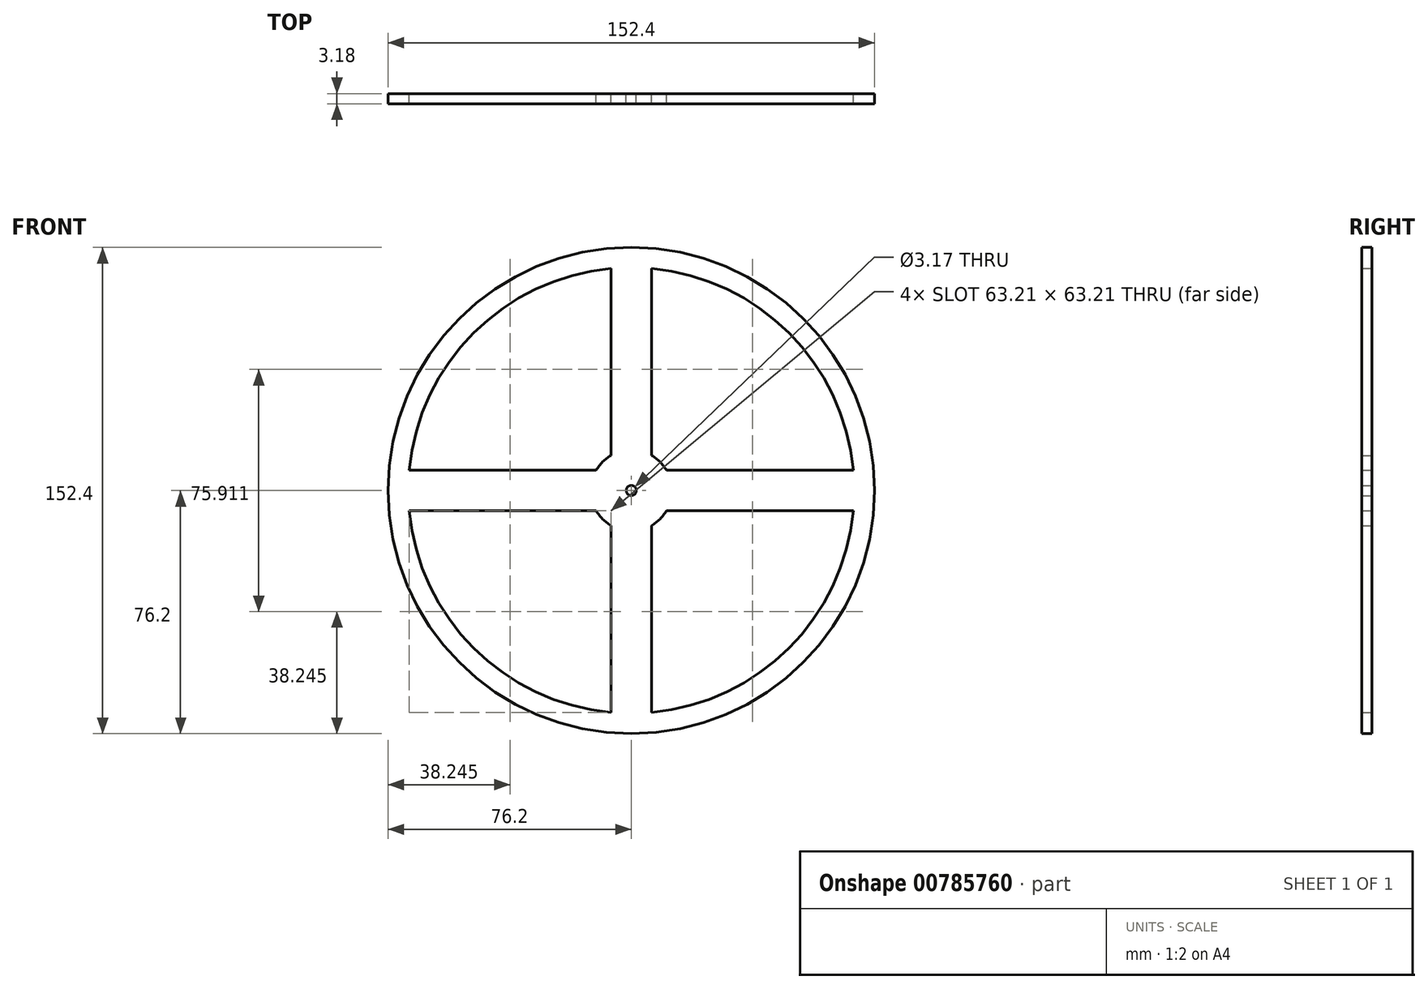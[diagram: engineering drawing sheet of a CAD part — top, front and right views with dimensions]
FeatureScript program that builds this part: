
annotation { "Feature Type Name" : "Feature", "Feature Type Description" : "" }
export const myFeature = defineFeature(function(context is Context, id is Id, definition is map)
    precondition{}
    {
        {
            var Q0;
            Q0=qCreatedBy(makeId("Front.planeOp"),FACE);
            var sketch = newSketch(context, id + "F0", { "sketchPlane" : qUnion([Q0])});
            skArc(sketch, "E0", {"start": v(-6.35, 69.56) * mm, "mid": v(-49.4, 49.4) * mm, "end": v(-69.56, 6.35) * mm});
            skCircle(sketch, "E1", {"center": v(0, 0) * mm, "radius": 1.59 * mm});
            skArc(sketch, "E2", {"start": v(-6.35, 11) * mm, "mid": v(-8.98, 8.98) * mm, "end": v(-11, 6.35) * mm});
            skLineSegment(sketch, "E3", {"start": v(-6.35, 69.56) * mm, "end": v(-6.35, 11) * mm});
            skLineSegment(sketch, "E4", {"start": v(6.35, 69.56) * mm, "end": v(6.35, 11) * mm});
            skLineSegment(sketch, "E5", {"start": v(-11, -6.35) * mm, "end": v(-69.56, -6.35) * mm});
            skLineSegment(sketch, "E6", {"start": v(-69.56, 6.35) * mm, "end": v(-69.56, -6.35) * mm, "construction": true});
            skLineSegment(sketch, "E7", {"start": v(-6.35, 69.56) * mm, "end": v(6.35, 69.56) * mm, "construction": true});
            skLineSegment(sketch, "E8", {"start": v(69.56, 6.35) * mm, "end": v(69.56, -6.35) * mm, "construction": true});
            skLineSegment(sketch, "E9", {"start": v(6.35, -69.56) * mm, "end": v(-6.35, -69.56) * mm, "construction": true});
            skLineSegment(sketch, "E10", {"start": v(-69.56, 6.35) * mm, "end": v(-11, 6.35) * mm});
            skLineSegment(sketch, "E11", {"start": v(-6.35, -11) * mm, "end": v(-6.35, -69.56) * mm});
            skLineSegment(sketch, "E12", {"start": v(6.35, -11) * mm, "end": v(6.35, -69.56) * mm});
            skLineSegment(sketch, "E13", {"start": v(11, 6.35) * mm, "end": v(69.56, 6.35) * mm});
            skLineSegment(sketch, "E14", {"start": v(11, -6.35) * mm, "end": v(69.56, -6.35) * mm});
            skArc(sketch, "E15.trimOffspring", {"start": v(-11, -6.35) * mm, "mid": v(-8.98, -8.98) * mm, "end": v(-6.35, -11) * mm});
            skArc(sketch, "E16.trimOffspring", {"start": v(6.35, -11) * mm, "mid": v(8.98, -8.98) * mm, "end": v(11, -6.35) * mm});
            skArc(sketch, "E17.trimOffspring", {"start": v(11, 6.35) * mm, "mid": v(8.98, 8.98) * mm, "end": v(6.35, 11) * mm});
            skCircle(sketch, "E18.0", {"center": v(0, 0) * mm, "radius": 76.2 * mm});
            skArc(sketch, "E19.trimOffspring", {"start": v(69.56, 6.35) * mm, "mid": v(49.4, 49.4) * mm, "end": v(6.35, 69.56) * mm});
            skArc(sketch, "E20.trimOffspring", {"start": v(6.35, -69.56) * mm, "mid": v(49.4, -49.4) * mm, "end": v(69.56, -6.35) * mm});
            skArc(sketch, "E21.trimOffspring", {"start": v(-69.56, -6.35) * mm, "mid": v(-49.4, -49.4) * mm, "end": v(-6.35, -69.56) * mm});
            skSolve(sketch);
        }
        {
            var Q0;
            Q0=makeQuery(id+"F0.imprint","IMPRINT",FACE,{"disambiguationData":[TD([[makeQuery(id+"F0.imprint","IMPRINT",EDGE,{"derivedFrom":sQuery(id+"F0.wireOp",EDGE,"E0")}),-1.0]])]});
            extrude(context, id + "F1", {"entities" : qUnion([Q0]), "depth" : 3.17 * mm, "offsetDistance" : 25.4 * mm});
        }
    });
